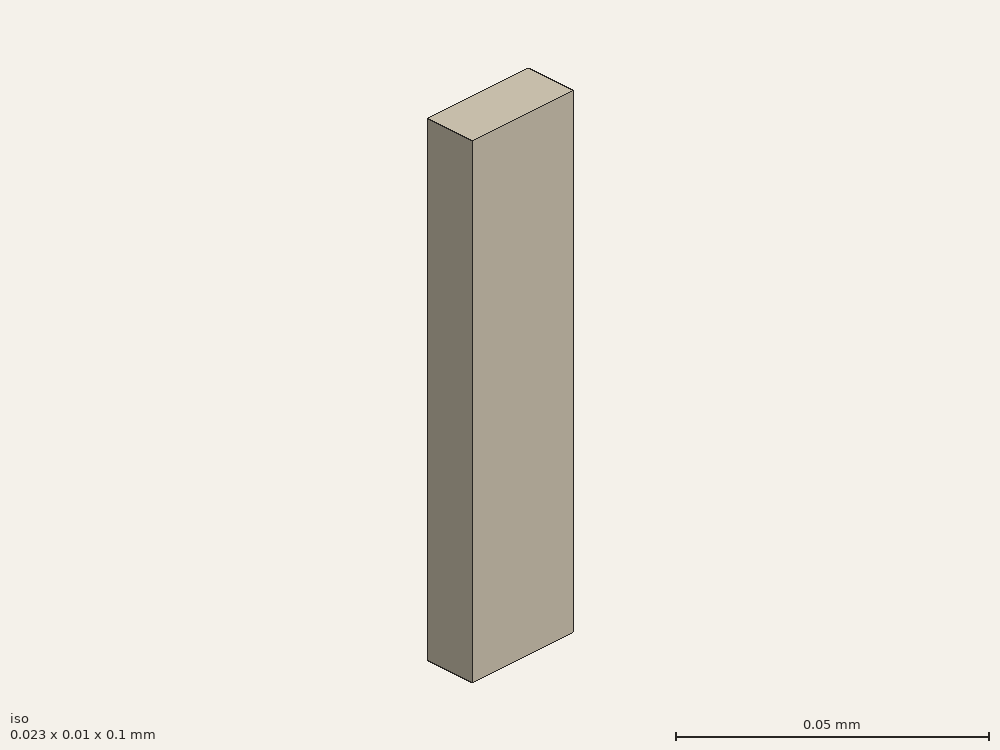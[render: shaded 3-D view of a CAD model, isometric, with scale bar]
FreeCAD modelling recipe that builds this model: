
FCSTD DOCUMENT  (FreeCAD 0.21R33694 (Git))
Label: straight
License: All rights reserved
LicenseURL: http://en.wikipedia.org/wiki/All_rights_reserved
objects: Part::Part2DObjectPython×5, App::FeaturePython×4, Part::Extrusion×1, Part::FeaturePython×1
note: 7 computed .brp shape members not serialized (recipe doc carries the construction recipe); baked Part::Feature solids carry a one-line shape summary decoded from their .brp

FEATURE [Part::Part2DObjectPython] Rectangle  # Draft 2D object (typed FeaturePython)
  Area = 232.258
  ChamferSize = 0
  Columns = 1
  FilletRadius = 0
  Height = 10.16
  Length = 22.86
  MakeFace = true
  Placement = pos=(-11.43,-5.08,0) rot=(0,0,1;0rad)
  Rows = 1
FEATURE [Part::Extrusion] Extrude
  Base = -> Rectangle
  Dir = (0,0,1)
  DirMode = 2
  FaceMakerClass = Part::FaceMakerBullseye
  LengthFwd = 100
  LengthRev = 0
  Solid = false
  Symmetric = false
FEATURE [Part::FeaturePython] Clone  label="Extrude001"  # Draft clone (typed FeaturePython)
  AttacherType = Attacher::AttachEngine3D
  Fuse = false
  Objects = -> [Extrude]
  Scale = (0.001,0.001,0.001)
FEATURE [Part::Part2DObjectPython] Rectangle001  label="_Pport1"  # Draft 2D object (typed FeaturePython)
  Area = 0.000232258
  ChamferSize = 0
  Columns = 1
  FilletRadius = 0
  Height = 0.01016
  Length = 0.02286
  MakeFace = true
  Placement = pos=(-0.01143,-0.00508,0.1) rot=(0,0,1;0rad)
  Rows = 1
FEATURE [Part::Part2DObjectPython] Line  label="_Pv1"  # Draft 2D object (typed FeaturePython)
  Area = 0
  ChamferSize = 0
  Closed = false
  End = (-1.8e-15,0.00508,0.1)
  FilletRadius = 0
  Length = 0.01016
  MakeFace = true
  Placement = pos=(0,-0.00508,0.1) rot=(0,0,1;0rad)
  Points = (2) [(0,0,0),(-1.77605e-15,0.01016,0)]
  Start = (0,-0.00508,0.1)
  Subdivisions = 0
FEATURE [Part::Part2DObjectPython] Rectangle002  label="_Pport2"  # Draft 2D object (typed FeaturePython)
  Area = 0.000232258
  ChamferSize = 0
  Columns = 1
  FilletRadius = 0
  Height = 0.01016
  Length = 0.02286
  MakeFace = true
  Placement = pos=(-0.01143,-0.00508,0) rot=(0,0,1;0rad)
  Rows = 1
FEATURE [Part::Part2DObjectPython] Line001  label="_Pv2"  # Draft 2D object (typed FeaturePython)
  Area = 0
  ChamferSize = 0
  Closed = false
  End = (0,0.00508,0)
  FilletRadius = 0
  Length = 0.01016
  MakeFace = true
  Placement = pos=(0,-0.00508,0) rot=(0,0,1;0rad)
  Points = (2) [(0,0,0),(3.1106e-19,0.01016,0)]
  Start = (0,-0.00508,0)
  Subdivisions = 0
FEATURE [App::FeaturePython] Text  label="_Sinput(PV){port1}"  # WARN: FeaturePython — macro-defined, semantics opaque (R4)
  Placement = pos=(0.0413747,-0.017509,0) rot=(0,0,1;0rad)
  Text = .
FEATURE [App::FeaturePython] Text001  label="_Soutput(PV){port2}"  # WARN: FeaturePython — macro-defined, semantics opaque (R4)
  Placement = pos=(0.0413747,-0.017509,0) rot=(0,0,1;0rad)
  Text = .
FEATURE [App::FeaturePython] Text002  label="_Linput(1,voltage){v1}"  # WARN: FeaturePython — macro-defined, semantics opaque (R4)
  Placement = pos=(0.0413747,-0.017509,0) rot=(0,0,1;0rad)
  Text = .
FEATURE [App::FeaturePython] Text003  label="_Loutput(2,voltage){v2}"  # WARN: FeaturePython — macro-defined, semantics opaque (R4)
  Placement = pos=(0.0413747,-0.017509,0) rot=(0,0,1;0rad)
  Text = .
